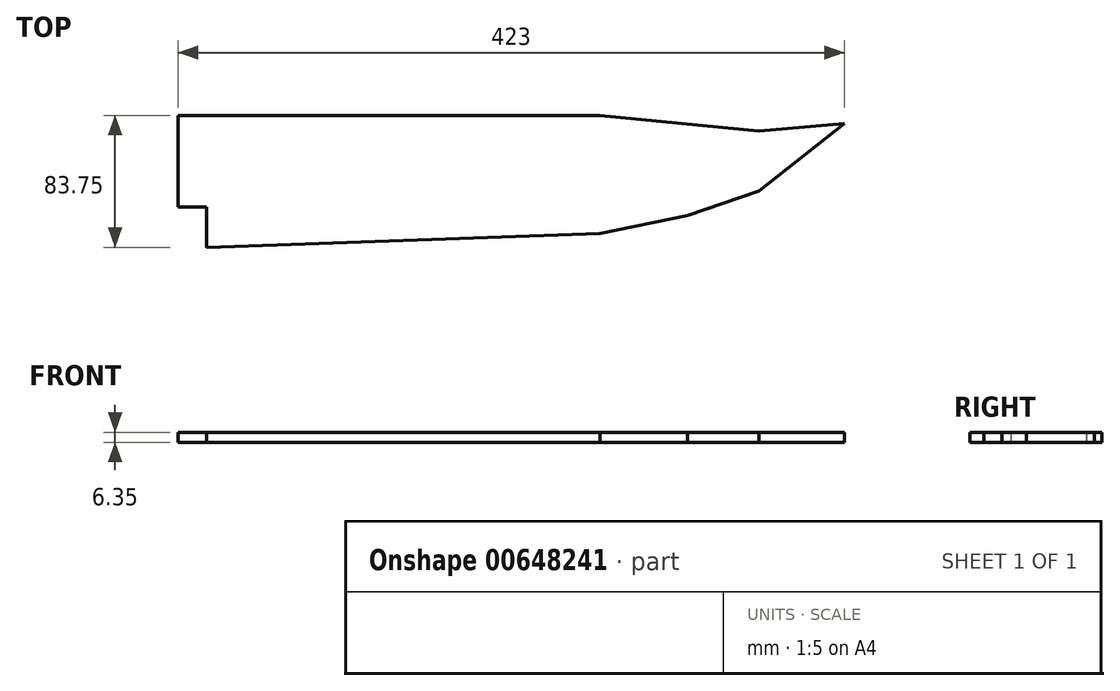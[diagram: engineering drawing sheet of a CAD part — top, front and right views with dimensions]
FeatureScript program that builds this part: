
annotation { "Feature Type Name" : "Feature", "Feature Type Description" : "" }
export const myFeature = defineFeature(function(context is Context, id is Id, definition is map)
    precondition{}
    {
        {
            var Q0;
            Q0=qCreatedBy(makeId("Top.planeOp"),FACE);
            var sketch = newSketch(context, id + "F0", { "sketchPlane" : qUnion([Q0])});
            skLineSegment(sketch, "E0.top", {"start": v(-166.39, 50.84) * mm, "end": v(83.61, 50.84) * mm});
            skLineSegment(sketch, "E0.left", {"start": v(-166.39, -32.9) * mm, "end": v(-166.39, -7.16) * mm});
            skLineSegment(sketch, "E1", {"start": v(-166.39, -32.9) * mm, "end": v(83.61, -24.16) * mm});
            skLineSegment(sketch, "E2", {"start": v(83.61, 50.84) * mm, "end": v(184.61, 40.84) * mm});
            skLineSegment(sketch, "E3", {"start": v(184.61, 40.84) * mm, "end": v(238.61, 45.84) * mm});
            skLineSegment(sketch, "E4", {"start": v(238.61, 45.84) * mm, "end": v(184.61, 2.84) * mm});
            skLineSegment(sketch, "E5", {"start": v(184.61, 2.84) * mm, "end": v(139, -12.8) * mm});
            skLineSegment(sketch, "E6", {"start": v(139, -12.8) * mm, "end": v(83.61, -24.16) * mm});
            skLineSegment(sketch, "E7", {"start": v(-166.39, 50.84) * mm, "end": v(-184.39, 50.84) * mm});
            skLineSegment(sketch, "E8", {"start": v(-184.39, 50.84) * mm, "end": v(-184.39, -7.16) * mm});
            skLineSegment(sketch, "E9", {"start": v(-184.39, -7.16) * mm, "end": v(-166.39, -7.16) * mm});
            skSolve(sketch);
        }
        {
            var Q0;
            Q0 = qSketchRegion(id + "F0", true);
            extrude(context, id + "F1", {"entities" : qUnion([Q0]), "depth" : 6.35 * mm, "offsetDistance" : 25 * mm});
        }
    });
